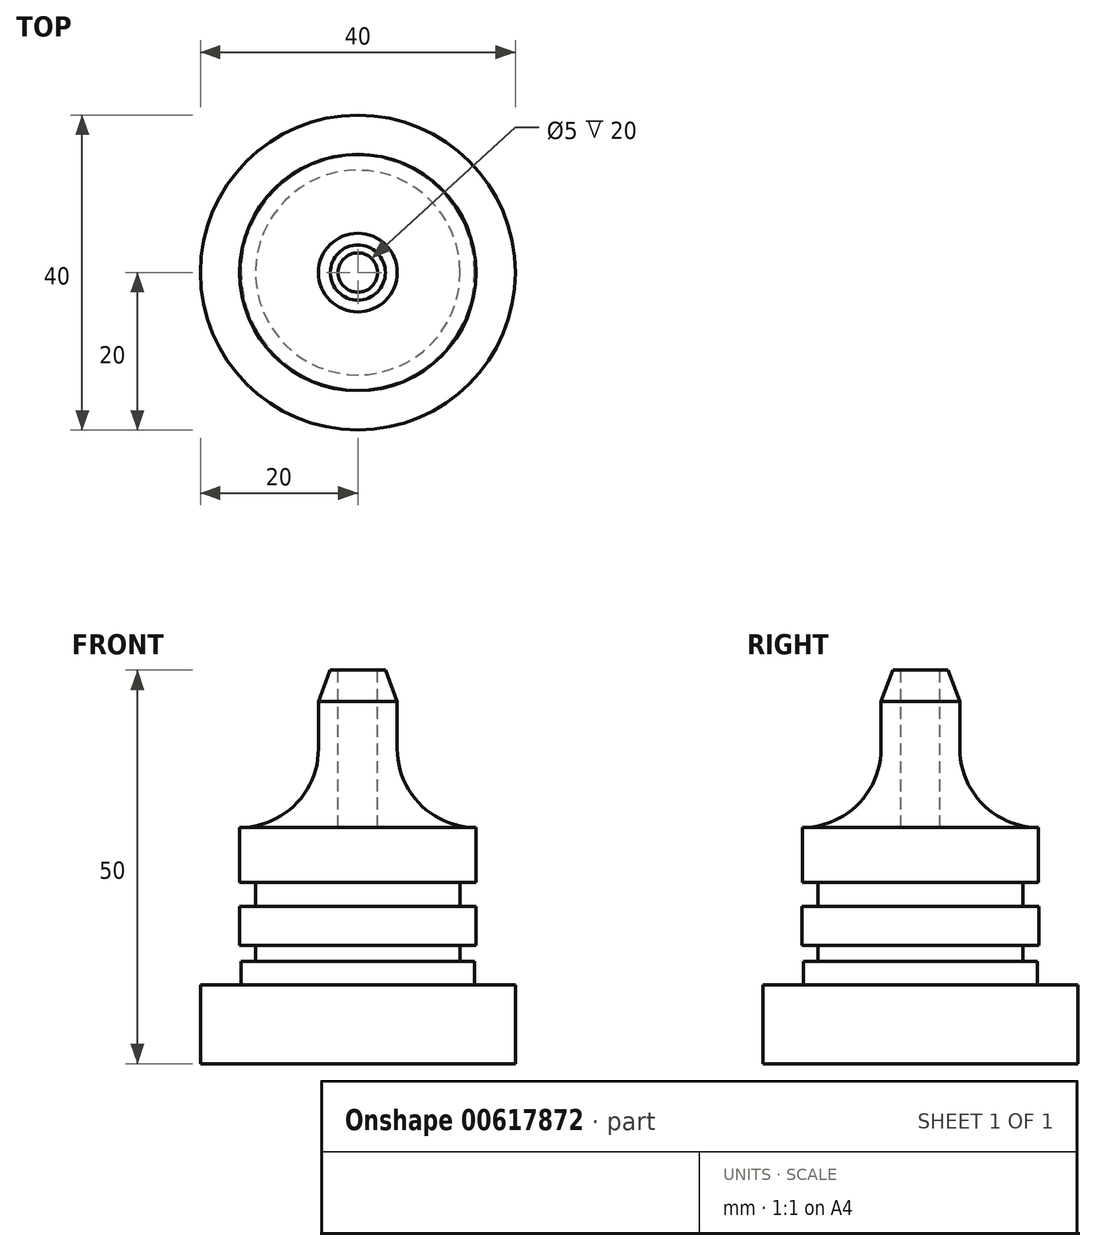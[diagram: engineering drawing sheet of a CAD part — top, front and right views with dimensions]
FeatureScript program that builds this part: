
annotation { "Feature Type Name" : "Feature", "Feature Type Description" : "" }
export const myFeature = defineFeature(function(context is Context, id is Id, definition is map)
    precondition{}
    {
        {
            var Q0;
            Q0=qCreatedBy(makeId("Front.planeOp"),FACE);
            var sketch = newSketch(context, id + "F0", { "sketchPlane" : qUnion([Q0])});
            skLineSegment(sketch, "E0.bottom", {"start": v(20, -21.44) * mm, "end": v(0, -21.44) * mm});
            skLineSegment(sketch, "E0.top", {"start": v(20, -11.44) * mm, "end": v(14.84, -11.44) * mm});
            skLineSegment(sketch, "E0.left", {"start": v(20, -21.44) * mm, "end": v(20, -11.44) * mm});
            skLineSegment(sketch, "E1.top", {"start": v(14.84, -8.44) * mm, "end": v(13, -8.44) * mm});
            skLineSegment(sketch, "E1.left", {"start": v(14.84, -11.44) * mm, "end": v(14.84, -8.44) * mm});
            skLineSegment(sketch, "E2.left", {"start": v(13, -8.44) * mm, "end": v(13, -6.44) * mm});
            skLineSegment(sketch, "E3.bottom", {"start": v(15.02, -6.44) * mm, "end": v(13, -6.44) * mm});
            skLineSegment(sketch, "E3.top", {"start": v(15.02, -1.44) * mm, "end": v(13, -1.44) * mm});
            skLineSegment(sketch, "E3.left", {"start": v(15.02, -6.44) * mm, "end": v(15.02, -1.44) * mm});
            skLineSegment(sketch, "E4.left", {"start": v(13, -1.44) * mm, "end": v(13, 1.56) * mm});
            skLineSegment(sketch, "E5.bottom", {"start": v(15, 1.56) * mm, "end": v(13, 1.56) * mm});
            skLineSegment(sketch, "E5.left", {"start": v(15, 1.56) * mm, "end": v(15, 8.56) * mm});
            skLineSegment(sketch, "E6", {"start": v(5, 18.56) * mm, "end": v(5, 24.56) * mm});
            skLineSegment(sketch, "E7", {"start": v(5, 24.56) * mm, "end": v(3.5, 28.56) * mm});
            skLineSegment(sketch, "E8", {"start": v(3.5, 28.56) * mm, "end": v(0, 28.56) * mm});
            skArc(sketch, "E9", {"start": v(5, 18.56) * mm, "mid": v(7.93, 11.5) * mm, "end": v(15, 8.56) * mm});
            skLineSegment(sketch, "E10", {"start": v(0, -21.44) * mm, "end": v(0, 28.56) * mm});
            skSolve(sketch);
        }
        {
            var Q0;
            Q0=makeQuery(id+"F0.imprint","IMPRINT",FACE,{"disambiguationData":[TD([[makeQuery(id+"F0.imprint","IMPRINT",EDGE,{"derivedFrom":sQuery(id+"F0.wireOp",EDGE,"E0.bottom")}),-1.0]])]});
            var Q1;
            Q1=sQuery(id+"F0.wireOp",EDGE,"E10");
            revolve(context, id + "F1", {"entities" : qUnion([Q0]), "axis" : qUnion([Q1]), "revolveType" : RevolveType.FULL});
        }
        {
            var Q0;
            Q0=makeQuery(id+"F1.opRevolve","SWEPT_FACE",FACE,{"disambiguationData":[OSD([sQuery(id+"F0.wireOp",EDGE,"E8")])]});
            var sketch = newSketch(context, id + "F2", { "sketchPlane" : qUnion([Q0])});
            skCircle(sketch, "E11", {"center": v(0, 0) * mm, "radius": 2.5 * mm});
            skSolve(sketch);
        }
        {
            var Q0;
            Q0=makeQuery(id+"F2.imprint","IMPRINT",FACE,{"disambiguationData":[TD([[makeQuery(id+"F2.imprint","IMPRINT",EDGE,{"derivedFrom":sQuery(id+"F2.wireOp",EDGE,"E11")}),1.0]])]});
            extrude(context, id + "F3", {"entities" : qUnion([Q0]), "operationType" : NewBodyOperationType.REMOVE, "oppositeDirection" : true, "depth" : 20 * mm, "offsetDistance" : 25 * mm});
        }
    });
